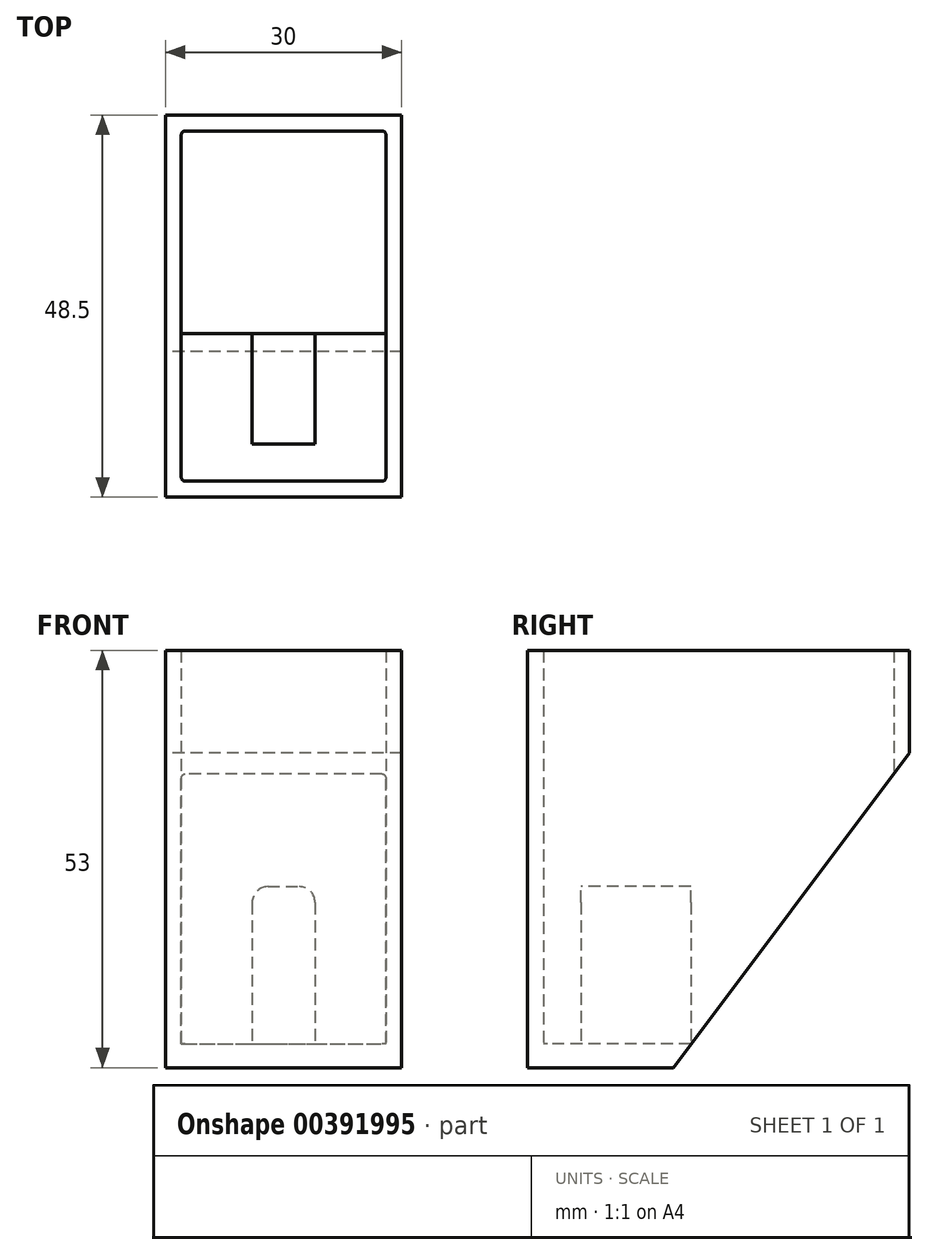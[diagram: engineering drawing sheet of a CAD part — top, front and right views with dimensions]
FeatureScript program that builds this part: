
annotation { "Feature Type Name" : "Feature", "Feature Type Description" : "" }
export const myFeature = defineFeature(function(context is Context, id is Id, definition is map)
    precondition{}
    {
        {
            var Q0;
            Q0=qCreatedBy(makeId("Top.planeOp"),FACE);
            var sketch = newSketch(context, id + "F0", { "sketchPlane" : qUnion([Q0])});
            skLineSegment(sketch, "E0.bottom", {"start": v(0, 0) * mm, "end": v(26, 0) * mm});
            skLineSegment(sketch, "E0.top", {"start": v(0, -44.5) * mm, "end": v(26, -44.5) * mm});
            skLineSegment(sketch, "E0.left", {"start": v(0, 0) * mm, "end": v(0, -44.5) * mm});
            skLineSegment(sketch, "E0.right", {"start": v(26, 0) * mm, "end": v(26, -44.5) * mm});
            skLineSegment(sketch, "E1.0", {"start": v(-2, -46.5) * mm, "end": v(28, -46.5) * mm});
            skLineSegment(sketch, "E1.1", {"start": v(-2, 2) * mm, "end": v(-2, -46.5) * mm});
            skLineSegment(sketch, "E1.2", {"start": v(-2, 2) * mm, "end": v(28, 2) * mm});
            skLineSegment(sketch, "E1.3", {"start": v(28, 2) * mm, "end": v(28, -46.5) * mm});
            skSolve(sketch);
        }
        {
            var Q0;
            Q0 = qSketchRegion(id + "F0", true);
            extrude(context, id + "F1", {"entities" : qUnion([Q0]), "depth" : 50 * mm});
        }
        {
            var Q0;
            Q0=makeQuery(id+"F1.opExtrude","CAP_FACE",FACE,{"disambiguationData":[OSD([sQuery(id+"F0.wireOp",EDGE,"E0.bottom"),sQuery(id+"F0.wireOp",EDGE,"E0.top"),sQuery(id+"F0.wireOp",EDGE,"E0.left"),sQuery(id+"F0.wireOp",EDGE,"E0.right"),sQuery(id+"F0.wireOp",EDGE,"E1.0"),sQuery(id+"F0.wireOp",EDGE,"E1.1"),sQuery(id+"F0.wireOp",EDGE,"E1.2"),sQuery(id+"F0.wireOp",EDGE,"E1.3")])],"isStart":true});
            var sketch = newSketch(context, id + "F2", { "sketchPlane" : qUnion([Q0])});
            skLineSegment(sketch, "E2.bottom", {"start": v(28, -2) * mm, "end": v(-2, -2) * mm});
            skLineSegment(sketch, "E2.top", {"start": v(28, 46.5) * mm, "end": v(-2, 46.5) * mm});
            skLineSegment(sketch, "E2.left", {"start": v(28, -2) * mm, "end": v(28, 46.5) * mm});
            skLineSegment(sketch, "E2.right", {"start": v(-2, -2) * mm, "end": v(-2, 46.5) * mm});
            skSolve(sketch);
        }
        {
            var Q0;
            Q0 = qSketchRegion(id + "F2", true);
            extrude(context, id + "F3", {"entities" : qUnion([Q0]), "operationType" : NewBodyOperationType.ADD, "depth" : 3 * mm});
        }
        {
            var Q0;
            Q0=makeQuery(id+"F3.boolean.opBoolean","MERGE",FACE,{"derivedFrom":[makeQuery(id+"F1.opExtrude","SWEPT_FACE",FACE,{"disambiguationData":[OSD([sQuery(id+"F0.wireOp",EDGE,"E1.1")])]}),makeQuery(id+"F3.opExtrude","SWEPT_FACE",FACE,{"disambiguationData":[OSD([sQuery(id+"F2.wireOp",EDGE,"E2.right")])]})]});
            var sketch = newSketch(context, id + "F4", { "sketchPlane" : qUnion([Q0])});
            skLineSegment(sketch, "E3", {"start": v(-2, -3) * mm, "end": v(28, -3) * mm});
            skLineSegment(sketch, "E4", {"start": v(-2, -3) * mm, "end": v(-2, 37) * mm});
            skLineSegment(sketch, "E5", {"start": v(-2, 37) * mm, "end": v(28, -3) * mm});
            skSolve(sketch);
        }
        {
            var Q0;
            Q0 = qSketchRegion(id + "F4", true);
            extrude(context, id + "F5", {"entities" : qUnion([Q0]), "operationType" : NewBodyOperationType.REMOVE, "oppositeDirection" : true, "depth" : 30 * mm});
        }
        {
            var Q0;
            Q0=makeQuery(id+"F3.opExtrude","CAP_FACE",FACE,{"disambiguationData":[OSD([sQuery(id+"F2.wireOp",EDGE,"E2.bottom"),sQuery(id+"F2.wireOp",EDGE,"E2.top"),sQuery(id+"F2.wireOp",EDGE,"E2.left"),sQuery(id+"F2.wireOp",EDGE,"E2.right")])],"isStart":true});
            var sketch = newSketch(context, id + "F6", { "sketchPlane" : qUnion([Q0])});
            skLineSegment(sketch, "E6", {"start": v(13, -25.75) * mm, "end": v(13, -41.43) * mm, "construction": true});
            skLineSegment(sketch, "E7.bottom", {"start": v(13, -25.75) * mm, "end": v(17, -25.75) * mm});
            skLineSegment(sketch, "E7.top", {"start": v(13, -39.75) * mm, "end": v(17, -39.75) * mm});
            skLineSegment(sketch, "E7.left", {"start": v(13, -25.75) * mm, "end": v(13, -39.75) * mm});
            skLineSegment(sketch, "E7.right", {"start": v(17, -25.75) * mm, "end": v(17, -39.75) * mm});
            skLineSegment(sketch, "E8.MirrorCS", {"start": v(13, -39.75) * mm, "end": v(9, -39.75) * mm});
            skLineSegment(sketch, "E9.MirrorCS", {"start": v(9, -25.75) * mm, "end": v(9, -39.75) * mm});
            skLineSegment(sketch, "E10.MirrorCS", {"start": v(13, -25.75) * mm, "end": v(9, -25.75) * mm});
            skSolve(sketch);
        }
        {
            var Q0;
            Q0 = qSketchRegion(id + "F6", true);
            extrude(context, id + "F7", {"entities" : qUnion([Q0]), "operationType" : NewBodyOperationType.ADD, "depth" : 20 * mm});
        }
        {
            var Q0;
            Q0=makeQuery(id+"F1.opExtrude","CAP_EDGE",EDGE,{"disambiguationData":[OSD([sQuery(id+"F0.wireOp",EDGE,"E0.left")])],"isStart":true});
            var Q1;
            Q1=makeQuery(id+"F1.opExtrude","CAP_EDGE",EDGE,{"disambiguationData":[OSD([sQuery(id+"F0.wireOp",EDGE,"E0.right")])],"isStart":true});
            var Q2;
            Q2=makeQuery(id+"F1.opExtrude","SWEPT_EDGE",EDGE,{"disambiguationData":[OSD([sQuery(id+"F0.wireOp",EDGE,"E0.bottom"),sQuery(id+"F0.wireOp",EDGE,"E0.left")])]});
            var Q3;
            Q3=makeQuery(id+"F1.opExtrude","SWEPT_EDGE",EDGE,{"disambiguationData":[OSD([sQuery(id+"F0.wireOp",EDGE,"E0.top"),sQuery(id+"F0.wireOp",EDGE,"E0.left")])]});
            var Q4;
            Q4=makeQuery(id+"F1.opExtrude","SWEPT_EDGE",EDGE,{"disambiguationData":[OSD([sQuery(id+"F0.wireOp",EDGE,"E0.top"),sQuery(id+"F0.wireOp",EDGE,"E0.right")])]});
            var Q5;
            Q5=makeQuery(id+"F1.opExtrude","SWEPT_EDGE",EDGE,{"disambiguationData":[OSD([sQuery(id+"F0.wireOp",EDGE,"E0.bottom"),sQuery(id+"F0.wireOp",EDGE,"E0.right")])]});
            fillet(context, id + "F8", {"entities" : qUnion([Q0, Q1, Q2, Q3, Q4, Q5]), "radius" : .5 * mm, "tangentPropagation" : true, "allowEdgeOverflow" : false});
        }
        {
            var Q0;
            Q0=makeQuery(id+"F7.opExtrude","CAP_EDGE",EDGE,{"disambiguationData":[OSD([sQuery(id+"F6.wireOp",EDGE,"E7.right")])],"isStart":false});
            var Q1;
            Q1=makeQuery(id+"F7.opExtrude","CAP_EDGE",EDGE,{"disambiguationData":[OSD([sQuery(id+"F6.wireOp",EDGE,"E9.MirrorCS")])],"isStart":false});
            var Q2;
            Q2=makeQuery(id+"F7.opExtrude","CAP_EDGE",EDGE,{"disambiguationData":[OSD([sQuery(id+"F6.wireOp",EDGE,"E7.right")])],"isStart":true});
            var Q3;
            Q3=makeQuery(id+"F7.opExtrude","CAP_EDGE",EDGE,{"disambiguationData":[OSD([sQuery(id+"F6.wireOp",EDGE,"E9.MirrorCS")])],"isStart":true});
            fillet(context, id + "F9", {"entities" : qUnion([Q0, Q1, Q2, Q3]), "radius" : 2 * mm, "tangentPropagation" : true, "allowEdgeOverflow" : false});
        }
    });
